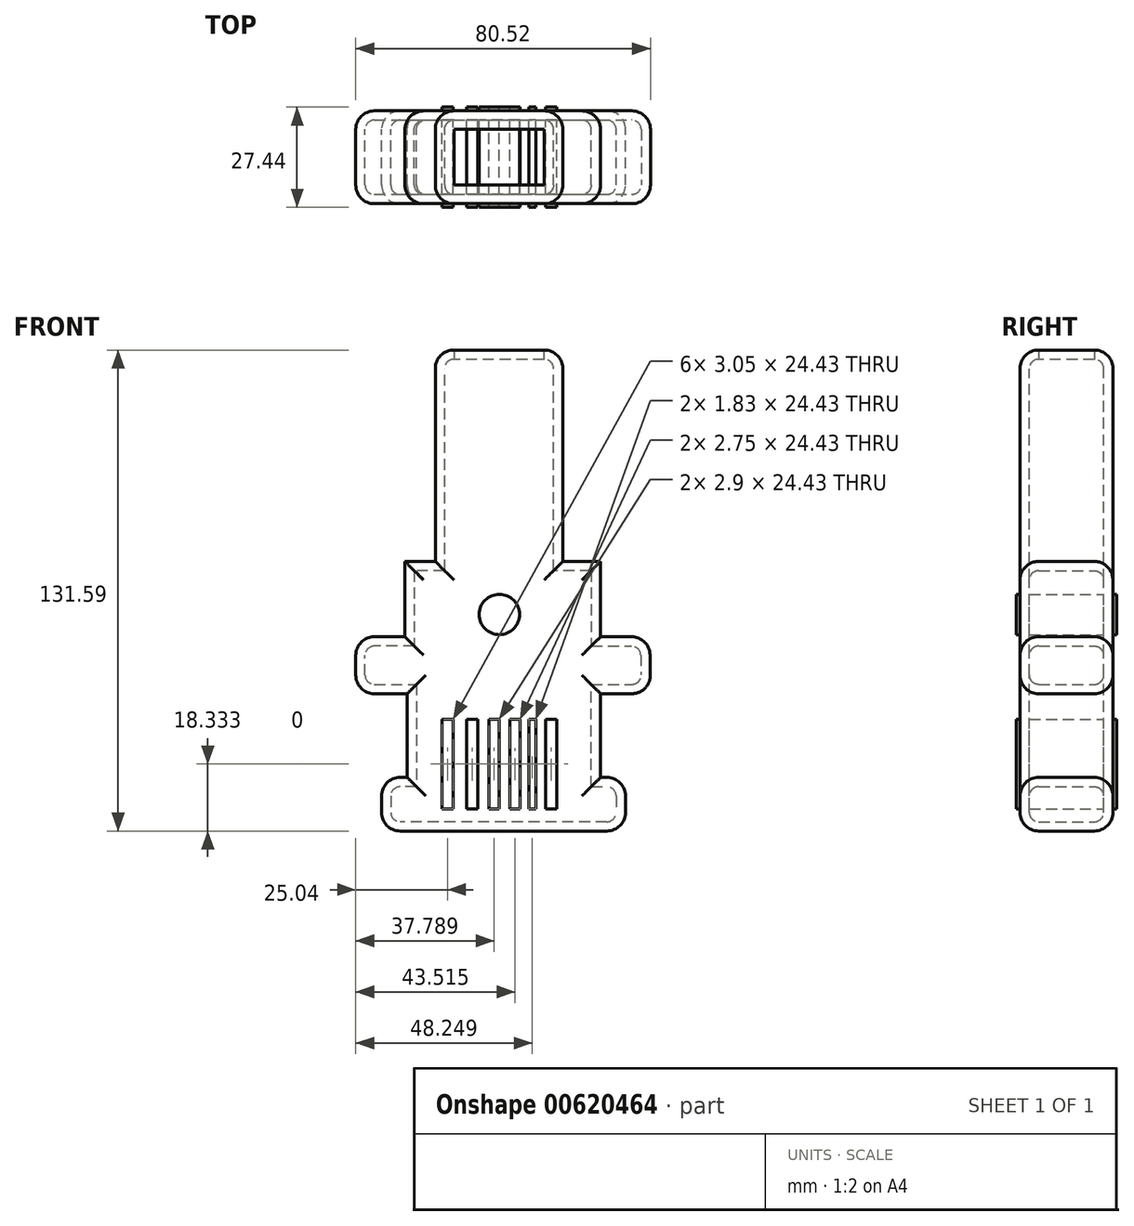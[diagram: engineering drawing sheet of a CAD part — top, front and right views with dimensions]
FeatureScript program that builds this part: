
annotation { "Feature Type Name" : "Feature", "Feature Type Description" : "" }
export const myFeature = defineFeature(function(context is Context, id is Id, definition is map)
    precondition{}
    {
        {
            var Q0;
            Q0=qCreatedBy(makeId("Front.planeOp"),FACE);
            var sketch = newSketch(context, id + "F0", { "sketchPlane" : qUnion([Q0])});
            skLineSegment(sketch, "E0", {"start": v(27.64, 0) * mm, "end": v(-25.8, 0) * mm});
            skLineSegment(sketch, "E1", {"start": v(-25.8, 0) * mm, "end": v(-25.8, -20.61) * mm});
            skLineSegment(sketch, "E2", {"start": v(27.64, 0) * mm, "end": v(27.64, -20.61) * mm});
            skLineSegment(sketch, "E3", {"start": v(-25.8, -20.61) * mm, "end": v(27.64, -20.61) * mm});
            skLineSegment(sketch, "E4", {"start": v(-25.8, -20.61) * mm, "end": v(-39.24, -20.61) * mm});
            skLineSegment(sketch, "E5", {"start": v(-39.24, -36.19) * mm, "end": v(-39.24, -20.61) * mm});
            skLineSegment(sketch, "E6", {"start": v(-39.24, -36.19) * mm, "end": v(41.38, -36.19) * mm});
            skLineSegment(sketch, "E7", {"start": v(27.64, -20.61) * mm, "end": v(41.07, -20.61) * mm});
            skLineSegment(sketch, "E8", {"start": v(41.07, -20.61) * mm, "end": v(41.38, -36.19) * mm});
            skLineSegment(sketch, "E9", {"start": v(-25.2, -36.19) * mm, "end": v(-25.2, -59.1) * mm});
            skLineSegment(sketch, "E10", {"start": v(-25.2, -59.1) * mm, "end": v(27.64, -59.1) * mm});
            skLineSegment(sketch, "E11", {"start": v(27.64, -59.1) * mm, "end": v(27.64, -36.19) * mm});
            skLineSegment(sketch, "E12", {"start": v(-25.2, -59.1) * mm, "end": v(-32.22, -59.1) * mm});
            skLineSegment(sketch, "E13", {"start": v(-32.22, -59.1) * mm, "end": v(-32.22, -73.76) * mm});
            skLineSegment(sketch, "E14", {"start": v(27.64, -59.1) * mm, "end": v(34.47, -59.1) * mm});
            skLineSegment(sketch, "E15", {"start": v(34.47, -59.1) * mm, "end": v(34.47, -73.76) * mm});
            skLineSegment(sketch, "E16", {"start": v(34.47, -73.76) * mm, "end": v(-32.22, -73.76) * mm});
            skLineSegment(sketch, "E17", {"start": v(-17.5, 0) * mm, "end": v(-17.5, 57.83) * mm});
            skLineSegment(sketch, "E18", {"start": v(17.35, 0) * mm, "end": v(17.35, 57.83) * mm});
            skLineSegment(sketch, "E19", {"start": v(-17.5, 57.83) * mm, "end": v(17.35, 57.83) * mm});
            skSolve(sketch);
        }
        {
            var Q0;
            Q0 = qSketchRegion(id + "F0", true);
            extrude(context, id + "F1", {"entities" : qUnion([Q0]), "endBound" : BoundingType.SYMMETRIC, "depth" : 25.4 * mm, "offsetDistance" : 25.4 * mm});
        }
        {
            var Q0;
            Q0=makeQuery(id+"F1.opExtrude","CAP_FACE",FACE,{"disambiguationData":[OSD([sQuery(id+"F0.wireOp",EDGE,"E0"),sQuery(id+"F0.wireOp",EDGE,"E1"),sQuery(id+"F0.wireOp",EDGE,"E2"),sQuery(id+"F0.wireOp",EDGE,"E4"),sQuery(id+"F0.wireOp",EDGE,"E5"),sQuery(id+"F0.wireOp",EDGE,"E6"),sQuery(id+"F0.wireOp",EDGE,"E7"),sQuery(id+"F0.wireOp",EDGE,"E8"),sQuery(id+"F0.wireOp",EDGE,"E9"),sQuery(id+"F0.wireOp",EDGE,"E11"),sQuery(id+"F0.wireOp",EDGE,"E12"),sQuery(id+"F0.wireOp",EDGE,"E13"),sQuery(id+"F0.wireOp",EDGE,"E14"),sQuery(id+"F0.wireOp",EDGE,"E15"),sQuery(id+"F0.wireOp",EDGE,"E16"),sQuery(id+"F0.wireOp",EDGE,"E17"),sQuery(id+"F0.wireOp",EDGE,"E18"),sQuery(id+"F0.wireOp",EDGE,"E19")])],"isStart":true});
            var Q1;
            Q1=makeQuery(id+"F1.opExtrude","SWEPT_FACE",FACE,{"disambiguationData":[OSD([sQuery(id+"F0.wireOp",EDGE,"E8")])]});
            var Q2;
            Q2=makeQuery(id+"F1.opExtrude","SWEPT_FACE",FACE,{"disambiguationData":[OSD([sQuery(id+"F0.wireOp",EDGE,"E15")])]});
            var Q3;
            Q3=makeQuery(id+"F1.opExtrude","CAP_FACE",FACE,{"disambiguationData":[OSD([sQuery(id+"F0.wireOp",EDGE,"E0"),sQuery(id+"F0.wireOp",EDGE,"E1"),sQuery(id+"F0.wireOp",EDGE,"E2"),sQuery(id+"F0.wireOp",EDGE,"E4"),sQuery(id+"F0.wireOp",EDGE,"E5"),sQuery(id+"F0.wireOp",EDGE,"E6"),sQuery(id+"F0.wireOp",EDGE,"E7"),sQuery(id+"F0.wireOp",EDGE,"E8"),sQuery(id+"F0.wireOp",EDGE,"E9"),sQuery(id+"F0.wireOp",EDGE,"E11"),sQuery(id+"F0.wireOp",EDGE,"E12"),sQuery(id+"F0.wireOp",EDGE,"E13"),sQuery(id+"F0.wireOp",EDGE,"E14"),sQuery(id+"F0.wireOp",EDGE,"E15"),sQuery(id+"F0.wireOp",EDGE,"E16"),sQuery(id+"F0.wireOp",EDGE,"E17"),sQuery(id+"F0.wireOp",EDGE,"E18"),sQuery(id+"F0.wireOp",EDGE,"E19")])],"isStart":false});
            var Q4;
            Q4=makeQuery(id+"F1.opExtrude","SWEPT_FACE",FACE,{"disambiguationData":[OSD([sQuery(id+"F0.wireOp",EDGE,"E5")])]});
            var Q5;
            Q5=makeQuery(id+"F1.opExtrude","SWEPT_FACE",FACE,{"disambiguationData":[OSD([sQuery(id+"F0.wireOp",EDGE,"E13")])]});
            var Q6;
            Q6=makeQuery(id+"F1.opExtrude","SWEPT_FACE",FACE,{"disambiguationData":[OSD([sQuery(id+"F0.wireOp",EDGE,"E19")])]});
            fillet(context, id + "F2", {"entities" : qUnion([Q0, Q1, Q2, Q3, Q4, Q5, Q6]), "radius" : 5.08 * mm, "tangentPropagation" : true, "allowEdgeOverflow" : false});
        }
        {
            var Q0;
            Q0=makeQuery(id+"F1.opExtrude","SWEPT_FACE",FACE,{"disambiguationData":[OSD([sQuery(id+"F0.wireOp",EDGE,"E19")])]});
            shell(context, id + "F3", {"entities" : qUnion([Q0]), "thickness" : 2.54 * mm});
        }
        {
            var Q0;
            Q0=qCreatedBy(makeId("Front.planeOp"),FACE);
            var sketch = newSketch(context, id + "F4", { "sketchPlane" : qUnion([Q0])});
            skCircle(sketch, "E20", {"center": v(0, -14.5) * mm, "radius": 5.52 * mm});
            skSolve(sketch);
        }
        {
            var Q0;
            Q0 = qSketchRegion(id + "F4", true);
            extrude(context, id + "F5", {"entities" : qUnion([Q0]), "operationType" : NewBodyOperationType.ADD, "endBound" : BoundingType.SYMMETRIC, "depth" : 27.43 * mm, "offsetDistance" : 25.4 * mm});
        }
        {
            var Q0;
            Q0=qCreatedBy(makeId("Front.planeOp"),FACE);
            var sketch = newSketch(context, id + "F6", { "sketchPlane" : qUnion([Q0])});
            skLineSegment(sketch, "E21.bottom", {"start": v(-15.73, -67.64) * mm, "end": v(-12.67, -67.64) * mm});
            skLineSegment(sketch, "E21.top", {"start": v(-15.73, -43.21) * mm, "end": v(-12.67, -43.21) * mm});
            skLineSegment(sketch, "E21.left", {"start": v(-15.73, -67.64) * mm, "end": v(-15.73, -43.21) * mm});
            skLineSegment(sketch, "E21.right", {"start": v(-12.67, -67.64) * mm, "end": v(-12.67, -43.21) * mm});
            skLineSegment(sketch, "E22.bottom", {"start": v(-9, -43.21) * mm, "end": v(-5.95, -43.21) * mm});
            skLineSegment(sketch, "E22.top", {"start": v(-9, -67.64) * mm, "end": v(-5.95, -67.64) * mm});
            skLineSegment(sketch, "E22.left", {"start": v(-9, -43.21) * mm, "end": v(-9, -67.64) * mm});
            skLineSegment(sketch, "E22.right", {"start": v(-5.95, -43.21) * mm, "end": v(-5.95, -67.64) * mm});
            skLineSegment(sketch, "E23.bottom", {"start": v(0, -43.21) * mm, "end": v(-2.9, -43.21) * mm});
            skLineSegment(sketch, "E23.top", {"start": v(0, -67.64) * mm, "end": v(-2.9, -67.64) * mm});
            skLineSegment(sketch, "E23.left", {"start": v(0, -43.21) * mm, "end": v(0, -67.64) * mm});
            skLineSegment(sketch, "E23.right", {"start": v(-2.9, -43.21) * mm, "end": v(-2.9, -67.64) * mm});
            skLineSegment(sketch, "E24.bottom", {"start": v(2.9, -43.21) * mm, "end": v(5.65, -43.21) * mm});
            skLineSegment(sketch, "E24.top", {"start": v(2.9, -67.64) * mm, "end": v(5.65, -67.64) * mm});
            skLineSegment(sketch, "E24.left", {"start": v(2.9, -43.21) * mm, "end": v(2.9, -67.64) * mm});
            skLineSegment(sketch, "E24.right", {"start": v(5.65, -43.21) * mm, "end": v(5.65, -67.64) * mm});
            skLineSegment(sketch, "E25.bottom", {"start": v(8.1, -43.21) * mm, "end": v(9.92, -43.21) * mm});
            skLineSegment(sketch, "E25.top", {"start": v(8.1, -67.64) * mm, "end": v(9.92, -67.64) * mm});
            skLineSegment(sketch, "E25.left", {"start": v(8.1, -43.21) * mm, "end": v(8.1, -67.64) * mm});
            skLineSegment(sketch, "E25.right", {"start": v(9.92, -43.21) * mm, "end": v(9.92, -67.64) * mm});
            skLineSegment(sketch, "E26.bottom", {"start": v(12.67, -43.21) * mm, "end": v(15.73, -43.21) * mm});
            skLineSegment(sketch, "E26.top", {"start": v(12.67, -67.64) * mm, "end": v(15.73, -67.64) * mm});
            skLineSegment(sketch, "E26.left", {"start": v(12.67, -43.21) * mm, "end": v(12.67, -67.64) * mm});
            skLineSegment(sketch, "E26.right", {"start": v(15.73, -43.21) * mm, "end": v(15.73, -67.64) * mm});
            skSolve(sketch);
        }
        {
            var Q0;
            Q0 = qSketchRegion(id + "F6", true);
            extrude(context, id + "F7", {"entities" : qUnion([Q0]), "operationType" : NewBodyOperationType.ADD, "endBound" : BoundingType.SYMMETRIC, "depth" : 27.43 * mm, "offsetDistance" : 25.4 * mm});
        }
    });
